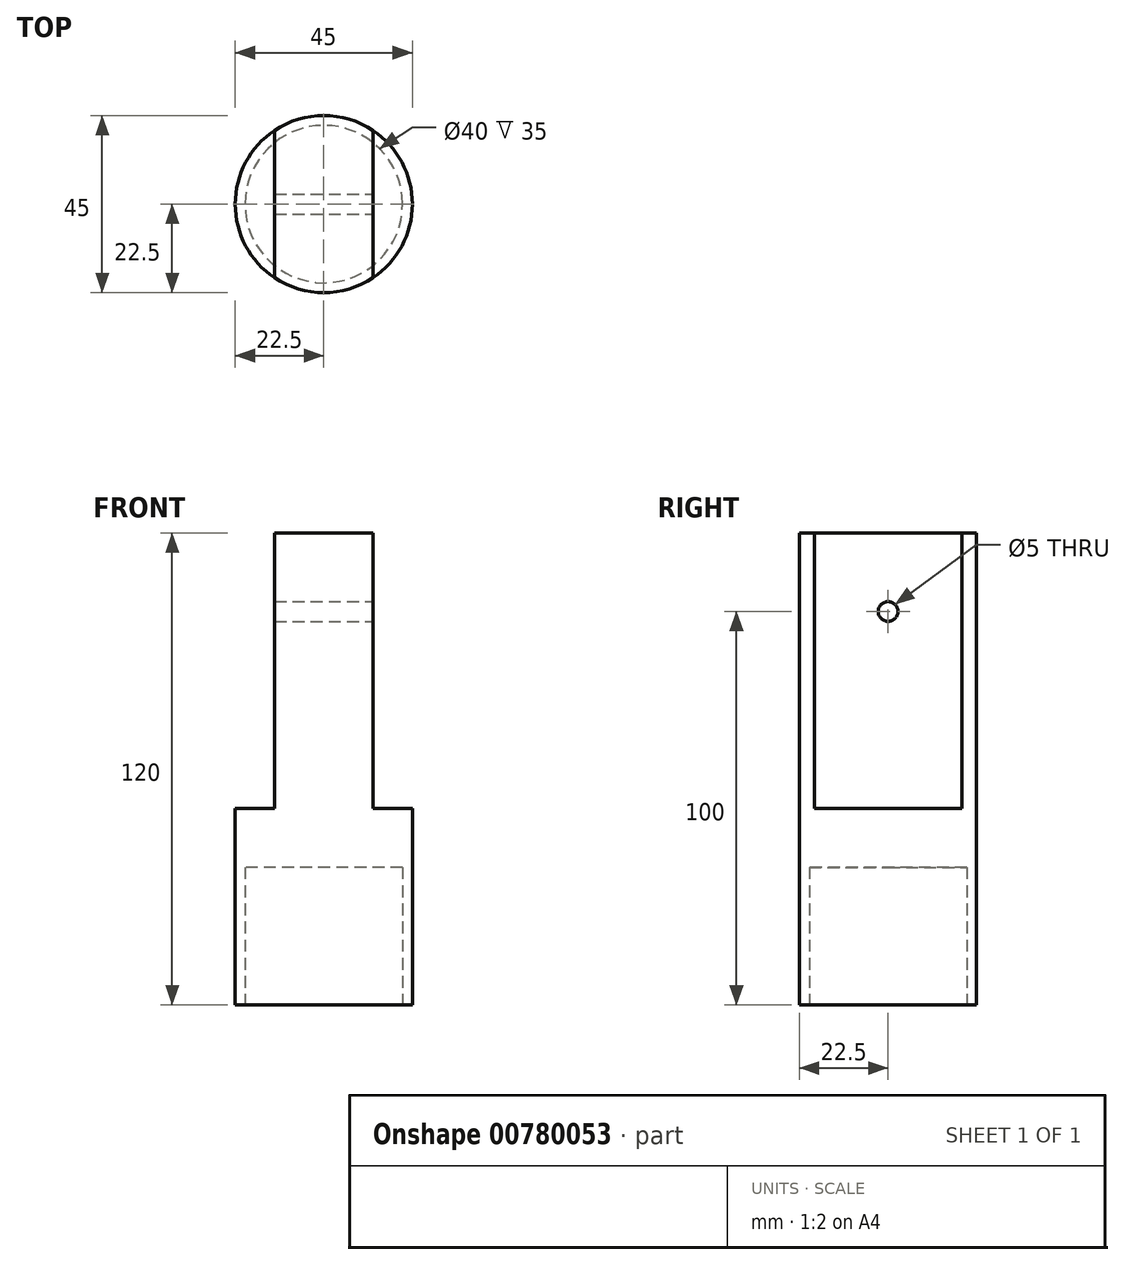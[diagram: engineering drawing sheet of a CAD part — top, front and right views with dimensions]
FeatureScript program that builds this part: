
annotation { "Feature Type Name" : "Feature", "Feature Type Description" : "" }
export const myFeature = defineFeature(function(context is Context, id is Id, definition is map)
    precondition{}
    {
        {
            var Q0;
            Q0=qCreatedBy(makeId("Top.planeOp"),FACE);
            var sketch = newSketch(context, id + "F0", { "sketchPlane" : qUnion([Q0])});
            skCircle(sketch, "E0", {"center": v(0, 0) * mm, "radius": 22.5 * mm});
            skSolve(sketch);
        }
        {
            var Q0;
            Q0=makeQuery(id+"F0.imprint","IMPRINT",FACE,{"disambiguationData":[TD([[makeQuery(id+"F0.imprint","IMPRINT",EDGE,{"derivedFrom":sQuery(id+"F0.wireOp",EDGE,"E0")}),1.0]])]});
            extrude(context, id + "F1", {"entities" : qUnion([Q0]), "depth" : 120 * mm, "offsetDistance" : 25 * mm});
        }
        {
            var Q0;
            Q0=makeQuery(id+"F1.opExtrude","CAP_FACE",FACE,{"disambiguationData":[OSD([sQuery(id+"F0.wireOp",EDGE,"E0")])],"isStart":false});
            var sketch = newSketch(context, id + "F2", { "sketchPlane" : qUnion([Q0])});
            skLineSegment(sketch, "E1", {"start": v(-12.5, 18.7) * mm, "end": v(-12.5, -18.7) * mm});
            skLineSegment(sketch, "E2", {"start": v(12.5, 18.7) * mm, "end": v(12.5, -18.7) * mm});
            skSolve(sketch);
        }
        {
            var Q0;
            {var subQ0=sQuery(id+"F2.wireOp",EDGE,"E1");Q0=makeQuery(id+"F2.imprint","IMPRINT",FACE,{"disambiguationData":[TD([[makeQuery(id+"F2.imprint","IMPRINT",EDGE,{"derivedFrom":subQ0}),-1.0]])]});}
            var Q1;
            {var subQ0=sQuery(id+"F2.wireOp",EDGE,"E2");Q1=makeQuery(id+"F2.imprint","IMPRINT",FACE,{"disambiguationData":[TD([[makeQuery(id+"F2.imprint","IMPRINT",EDGE,{"derivedFrom":subQ0}),1.0]])]});}
            extrude(context, id + "F3", {"entities" : qUnion([Q0, Q1]), "operationType" : NewBodyOperationType.REMOVE, "oppositeDirection" : true, "depth" : 70 * mm, "offsetDistance" : 25 * mm});
        }
        {
            var Q0;
            Q0=makeQuery(id+"F0.imprint","IMPRINT",FACE,{"disambiguationData":[TD([[makeQuery(id+"F0.imprint","IMPRINT",EDGE,{"derivedFrom":sQuery(id+"F0.wireOp",EDGE,"E0")}),1.0]])]});
            var sketch = newSketch(context, id + "F4", { "sketchPlane" : qUnion([Q0])});
            skCircle(sketch, "E3", {"center": v(0, 0) * mm, "radius": 20 * mm});
            skSolve(sketch);
        }
        {
            var Q0;
            Q0=qSketchRegion(id+"F4",true);
            extrude(context, id + "F5", {"entities" : qUnion([Q0]), "operationType" : NewBodyOperationType.REMOVE, "depth" : 35 * mm, "offsetDistance" : 25 * mm});
        }
        {
            var Q0;
            Q0=qCreatedBy(makeId("Right.planeOp"),FACE);
            cPlane(context, id + "F6", {"entities" : qUnion([Q0]), "cplaneType" : CPlaneType.OFFSET, "offset" : 22.5 * mm, "width" : 150 * mm, "height" : 150 * mm});
        }
        {
            var Q0;
            Q0=qCreatedBy(id+"F6.planeOp",FACE);
            var sketch = newSketch(context, id + "F7", { "sketchPlane" : qUnion([Q0])});
            skLineSegment(sketch, "E4", {"start": v(-18.7, 100) * mm, "end": v(18.7, 100) * mm});
            skPoint(sketch, "E5", {"position": v(0, 100) * mm});
            skSolve(sketch);
        }
        {
            var Q0;
            Q0=sQuery(id+"F7.wireOp",VERTEX,"E5");
            var Q1;
            Q1=makeQuery(id+"F1.opExtrude","SWEPT_BODY",BODY,{"disambiguationData":[OSD([sQuery(id+"F0.wireOp",EDGE,"E0")])]});
            hole(context, id + "F8", {"style" : HoleStyle.SIMPLE, "endStyle" : HoleEndStyle.THROUGH, "holeDiameter" : 5 * mm, "majorDiameter" : 5 * mm, "isTappedThrough" : true, "tappedDepth" : 12 * mm, "tapClearance" : 3, "locations" : qUnion([Q0]), "scope" : qUnion([Q1])});
        }
    });
